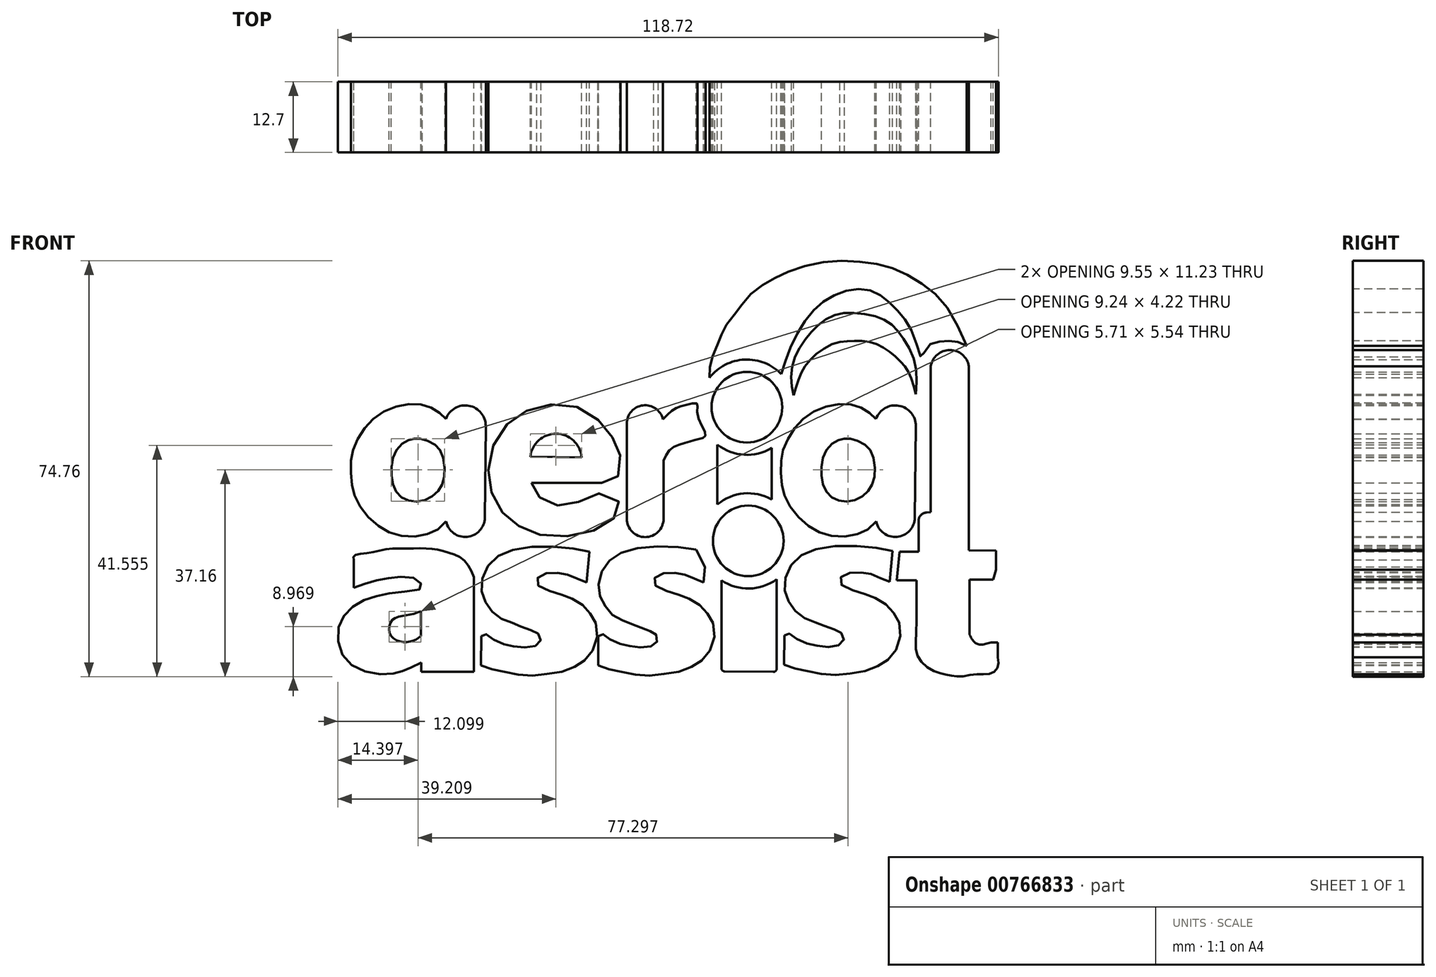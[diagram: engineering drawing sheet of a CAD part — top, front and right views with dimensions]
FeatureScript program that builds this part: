
annotation { "Feature Type Name" : "Feature", "Feature Type Description" : "" }
export const myFeature = defineFeature(function(context is Context, id is Id, definition is map)
    precondition{}
    {
        {
            var Q0;
            Q0=qCreatedBy(makeId("Front.planeOp"),FACE);
            var sketch = newSketch(context, id + "F0", { "sketchPlane" : qUnion([Q0])});
            skFitSpline(sketch, "E0", {"points": [v(-44.08, 9.66) * mm, v(-45.28, 10.79) * mm, v(-47.25, 11.85) * mm, v(-49.88, 12.36) * mm, v(-53.47, 11.74) * mm, v(-56.78, 9.94) * mm, v(-59.07, 7.42) * mm, v(-60.64, 4.45) * mm, v(-61.15, 1.98) * mm, v(-61.1, -1.44) * mm, v(-60.59, -3.9) * mm, v(-58.9, -6.99) * mm, v(-56.1, -9.68) * mm, v(-53.08, -11.2) * mm, v(-49.26, -11.47) * mm, v(-46.18, -10.57) * mm, v(-44.05, -8.78) * mm, v(-41.64, -2.84) * mm], "startDerivative": vector(-26.95, 27.22) * mm, "endDerivative": vector(26.9, 83.07) * mm});
            skArc(sketch, "E1.0.endCap", {"start": v(-37.1, -8.1) * mm, "mid": v(-40.27, -11.57) * mm, "end": v(-44.06, -8.8) * mm});
            skLineSegment(sketch, "E1.0.left", {"start": v(-36.93, 8.34) * mm, "end": v(-37.1, -8.1) * mm});
            skArc(sketch, "E2", {"start": v(-36.93, 8.34) * mm, "mid": v(-39.95, 12.01) * mm, "end": v(-44.08, 9.66) * mm});
            skFitSpline(sketch, "E3", {"points": [v(-49.79, 6.08) * mm, v(-51.15, 5.71) * mm, v(-52.94, 4.16) * mm, v(-53.82, 1.44) * mm, v(-53.77, -1.42) * mm, v(-52.8, -3.75) * mm, v(-51, -4.96) * mm, v(-48.63, -5.16) * mm, v(-46.25, -4.04) * mm, v(-44.89, -2.4) * mm, v(-44.3, 0) * mm, v(-44.8, 3.33) * mm, v(-46.1, 5.03) * mm, v(-48.33, 6) * mm, v(-49.79, 6.08) * mm]});
            skLineSegment(sketch, "E4", {"start": v(-28.93, 2.84) * mm, "end": v(-19.7, 2.74) * mm});
            skArc(sketch, "E5", {"start": v(-19.7, 2.74) * mm, "mid": v(-24.27, 6.97) * mm, "end": v(-28.93, 2.84) * mm});
            skLineSegment(sketch, "E6", {"start": v(-28.74, -1.84) * mm, "end": v(-16.09, -1.84) * mm});
            skFitSpline(sketch, "E7", {"points": [v(-16.09, -1.84) * mm, v(-13.72, -1.34) * mm, v(-12.94, 0) * mm, v(-12.76, 3.12) * mm, v(-13.6, 5.34) * mm, v(-14.98, 7.55) * mm, v(-17.38, 9.96) * mm, v(-20.8, 11.9) * mm, v(-24.86, 12.27) * mm, v(-29.02, 11.34) * mm, v(-31.98, 9.68) * mm, v(-34.57, 6.9) * mm, v(-36.04, 3.12) * mm, v(-36.45, -0.54) * mm, v(-35.92, -3.57) * mm, v(-34.42, -6.54) * mm, v(-32.43, -8.6) * mm, v(-30.06, -10.14) * mm, v(-26.74, -11.31) * mm, v(-22.05, -11.44) * mm, v(-17.68, -10.46) * mm, v(-14.42, -8.64) * mm, v(-13, -7.08) * mm, v(-13.25, -4.86) * mm, v(-16.09, -3.69) * mm, v(-18.98, -4.73) * mm, v(-21.66, -5.77) * mm, v(-24.46, -5.84) * mm, v(-26.74, -4.8) * mm, v(-28.1, -3.5) * mm, v(-28.74, -1.84) * mm], "startDerivative": vector(116.89, 0) * mm, "endDerivative": vector(-21.57, 62.43) * mm});
            skArc(sketch, "E8.0.startCap", {"start": v(-11.58, 8.8) * mm, "mid": v(-8.69, 12.07) * mm, "end": v(-5.08, 9.6) * mm});
            skArc(sketch, "E8.0.endCap", {"start": v(-4.98, -8.32) * mm, "mid": v(-8.28, -11.62) * mm, "end": v(-11.58, -8.32) * mm});
            skLineSegment(sketch, "E8.0.left", {"start": v(-4.98, 2.12) * mm, "end": v(-4.98, -8.32) * mm});
            skLineSegment(sketch, "E8.0.right", {"start": v(-11.58, 8.8) * mm, "end": v(-11.58, -8.32) * mm});
            skFitSpline(sketch, "E9", {"points": [v(-5.08, 9.6) * mm, v(-3.02, 11.46) * mm, v(-0.9, 12.17) * mm, v(1.06, 12.4) * mm, v(1.06, 10.52) * mm, v(2.55, 6.99) * mm, v(2.16, 6.28) * mm, v(0.75, 5.89) * mm, v(-0.98, 5.34) * mm, v(-3.5, 4.4) * mm, v(-4.98, 2.12) * mm], "startDerivative": vector(17.8, 19.08) * mm, "endDerivative": vector(-10.39, -23.26) * mm});
            skCircle(sketch, "E10", {"center": v(10.02, 11.75) * mm, "radius": 6.35 * mm});
            skArc(sketch, "E11", {"start": v(4.7, 5.02) * mm, "mid": v(9.48, 3.2) * mm, "end": v(14.45, 4.42) * mm});
            skFitSpline(sketch, "E12", {"points": [v(3.3, 17.09) * mm, v(3.37, 19.33) * mm, v(4.23, 21.82) * mm, v(5.24, 24.32) * mm, v(6.32, 26.56) * mm, v(8.2, 28.96) * mm, v(10.43, 31.79) * mm, v(13.78, 34.27) * mm, v(17.63, 36.16) * mm, v(23.98, 37.87) * mm, v(30.58, 37.87) * mm, v(35.98, 36.85) * mm, v(40.86, 34.36) * mm, v(45.32, 30.59) * mm, v(49.52, 22.79) * mm], "startDerivative": vector(-2.37, 43.6) * mm, "endDerivative": vector(38.1, -85.11) * mm});
            skFitSpline(sketch, "E13", {"points": [v(49.52, 22.79) * mm, v(47.2, 23.65) * mm, v(44.98, 23.56) * mm, v(42.58, 22.79) * mm, v(41.37, 20.77) * mm, v(40.06, 24.45) * mm, v(37.83, 28.27) * mm, v(35.38, 30.85) * mm, v(32.46, 32.65) * mm, v(28.6, 32.82) * mm, v(24.5, 31.19) * mm, v(21.06, 28.1) * mm, v(17.98, 22.79) * mm, v(16.2, 17.69) * mm], "startDerivative": vector(-37.27, 17.9) * mm, "endDerivative": vector(-16.52, -54.42) * mm});
            skCircle(sketch, "E14", {"center": v(10.24, -12.3) * mm, "radius": 6.35 * mm});
            skArc(sketch, "E15", {"start": v(5.42, -19.38) * mm, "mid": v(10.43, -20.87) * mm, "end": v(15.38, -19.16) * mm});
            skLineSegment(sketch, "E16", {"start": v(4.7, 5.02) * mm, "end": v(4.7, -5.75) * mm});
            skLineSegment(sketch, "E17", {"start": v(14.45, 4.42) * mm, "end": v(14.45, -4.83) * mm});
            skArc(sketch, "E18.trimOffspring", {"start": v(16.2, 17.69) * mm, "mid": v(9.62, 20.32) * mm, "end": v(3.3, 17.09) * mm});
            skLineSegment(sketch, "E19", {"start": v(5.42, -19.38) * mm, "end": v(5.42, -35.14) * mm});
            skLineSegment(sketch, "E20", {"start": v(6.04, -35.77) * mm, "end": v(14.74, -35.86) * mm});
            skLineSegment(sketch, "E21", {"start": v(15.38, -35.23) * mm, "end": v(15.38, -19.16) * mm});
            skPoint(sketch, "E22.visualSharp", {"position": v(5.42, -35.76) * mm});
            skArc(sketch, "E22.filletArc", {"start": v(5.42, -35.14) * mm, "mid": v(5.6, -35.58) * mm, "end": v(6.04, -35.77) * mm});
            skPoint(sketch, "E23.visualSharp", {"position": v(15.38, -35.87) * mm});
            skArc(sketch, "E23.filletArc", {"start": v(14.74, -35.86) * mm, "mid": v(15.19, -35.68) * mm, "end": v(15.38, -35.23) * mm});
            skArc(sketch, "E24.trimOffspring", {"start": v(14.45, -4.83) * mm, "mid": v(9.43, -3.76) * mm, "end": v(4.7, -5.75) * mm});
            skFitSpline(sketch, "E25", {"points": [v(18.39, 13.87) * mm, v(17.96, 17.1) * mm, v(18.7, 20.85) * mm, v(20.64, 24.07) * mm, v(22.9, 26.54) * mm, v(25.9, 28.37) * mm, v(29.55, 28.7) * mm, v(33.63, 27.94) * mm, v(36.32, 26.33) * mm, v(38.36, 23.75) * mm, v(40.29, 19.46) * mm, v(40.4, 14.09) * mm], "startDerivative": vector(-7.7, 37.27) * mm, "endDerivative": vector(-3.75, -50.87) * mm});
            skFitSpline(sketch, "E26", {"points": [v(40.4, 14.09) * mm, v(39.22, 17.74) * mm, v(37.82, 19.78) * mm, v(35.35, 21.93) * mm, v(32.34, 23.43) * mm, v(29.02, 23.64) * mm, v(25.69, 23.22) * mm, v(21.5, 20.42) * mm, v(19.67, 17.63) * mm, v(18.39, 13.87) * mm], "startDerivative": vector(-9.3, 34.22) * mm, "endDerivative": vector(-10.28, -33.52) * mm});
            skFitSpline(sketch, "E27", {"points": [v(33.22, 9.66) * mm, v(32.01, 10.79) * mm, v(30.05, 11.85) * mm, v(27.42, 12.36) * mm, v(23.83, 11.74) * mm, v(20.52, 9.94) * mm, v(18.22, 7.42) * mm, v(16.65, 4.45) * mm, v(16.15, 1.98) * mm, v(16.2, -1.44) * mm, v(16.7, -3.9) * mm, v(18.4, -6.99) * mm, v(21.2, -9.68) * mm, v(24.22, -11.2) * mm, v(28.03, -11.47) * mm, v(31.12, -10.57) * mm, v(33.25, -8.78) * mm, v(35.66, -2.84) * mm], "startDerivative": vector(-26.95, 27.22) * mm, "endDerivative": vector(26.9, 83.07) * mm});
            skArc(sketch, "E28.0.endCap", {"start": v(40.2, -8.1) * mm, "mid": v(37.03, -11.57) * mm, "end": v(33.24, -8.8) * mm});
            skLineSegment(sketch, "E28.0.left", {"start": v(40.37, 8.34) * mm, "end": v(40.2, -8.1) * mm});
            skArc(sketch, "E29", {"start": v(40.37, 8.34) * mm, "mid": v(37.35, 12.01) * mm, "end": v(33.22, 9.66) * mm});
            skFitSpline(sketch, "E30", {"points": [v(27.51, 6.08) * mm, v(26.15, 5.71) * mm, v(24.35, 4.16) * mm, v(23.48, 1.44) * mm, v(23.53, -1.42) * mm, v(24.5, -3.75) * mm, v(26.3, -4.96) * mm, v(28.67, -5.16) * mm, v(31.05, -4.04) * mm, v(32.4, -2.4) * mm, v(33, 0) * mm, v(32.5, 3.33) * mm, v(31.2, 5.03) * mm, v(28.96, 6) * mm, v(27.51, 6.08) * mm]});
            skLineSegment(sketch, "E31", {"start": v(49.9, 19.12) * mm, "end": v(49.9, -13.98) * mm});
            skLineSegment(sketch, "E32", {"start": v(49.9, -13.98) * mm, "end": v(54.8, -14.03) * mm});
            skLineSegment(sketch, "E33", {"start": v(54.8, -14.03) * mm, "end": v(54.8, -17.5) * mm});
            skLineSegment(sketch, "E34", {"start": v(54.8, -17.5) * mm, "end": v(54.29, -19.29) * mm});
            skLineSegment(sketch, "E35", {"start": v(54.29, -19.29) * mm, "end": v(50.04, -19.24) * mm});
            skLineSegment(sketch, "E36", {"start": v(50.04, -19.24) * mm, "end": v(50.04, -29.15) * mm});
            skFitSpline(sketch, "E37", {"points": [v(50.04, -29.15) * mm, v(50.72, -30.31) * mm, v(51.8, -30.93) * mm, v(53.9, -30.54) * mm], "startDerivative": vector(1.89, -4.02) * mm, "endDerivative": vector(5.77, 1.79) * mm});
            skLineSegment(sketch, "E38", {"start": v(53.9, -30.54) * mm, "end": v(55.08, -30.54) * mm});
            skLineSegment(sketch, "E39", {"start": v(55.08, -30.54) * mm, "end": v(55.08, -33.26) * mm});
            skFitSpline(sketch, "E40", {"points": [v(55.08, -33.26) * mm, v(55.08, -35.03) * mm, v(53.74, -36.18) * mm, v(51.24, -36.28) * mm, v(48.22, -36.7) * mm, v(46.13, -36.39) * mm, v(43.74, -35.76) * mm, v(40.82, -33.26) * mm, v(40.4, -29.83) * mm, v(40.5, -19.4) * mm], "startDerivative": vector(3.8, -22.5) * mm, "endDerivative": vector(0.14, 58.8) * mm});
            skLineSegment(sketch, "E41", {"start": v(40.5, -19.4) * mm, "end": v(36.97, -19.4) * mm});
            skLineSegment(sketch, "E42", {"start": v(36.97, -19.4) * mm, "end": v(37.44, -14.23) * mm});
            skLineSegment(sketch, "E43", {"start": v(37.44, -14.23) * mm, "end": v(40.85, -14.23) * mm});
            skLineSegment(sketch, "E44", {"start": v(40.85, -14.23) * mm, "end": v(40.85, -8.72) * mm});
            skArc(sketch, "E45", {"start": v(42.31, -7.18) * mm, "mid": v(41.27, -7.66) * mm, "end": v(40.85, -8.72) * mm});
            skLineSegment(sketch, "E46", {"start": v(42.31, -7.18) * mm, "end": v(43.07, -7.15) * mm});
            skLineSegment(sketch, "E47", {"start": v(43.07, -7.15) * mm, "end": v(43.07, 19.12) * mm});
            skArc(sketch, "E48", {"start": v(49.9, 19.12) * mm, "mid": v(46.49, 22.03) * mm, "end": v(43.07, 19.12) * mm});
            skLineSegment(sketch, "E49", {"start": v(-60.64, -20.7) * mm, "end": v(-60.64, -15.71) * mm});
            skFitSpline(sketch, "E50", {"points": [v(-60.64, -15.71) * mm, v(-60.64, -15) * mm, v(-58.31, -14.49) * mm, v(-54.56, -13.77) * mm, v(-50.16, -13.64) * mm, v(-46.67, -13.7) * mm, v(-43.76, -14.36) * mm, v(-40.91, -15.71) * mm, v(-39.05, -18.82) * mm], "startDerivative": vector(-3.73, 12.95) * mm, "endDerivative": vector(10.17, -25.55) * mm});
            skLineSegment(sketch, "E51", {"start": v(-39.05, -18.82) * mm, "end": v(-39.05, -35.8) * mm});
            skLineSegment(sketch, "E52", {"start": v(-39.05, -35.8) * mm, "end": v(-48.55, -35.8) * mm});
            skLineSegment(sketch, "E53", {"start": v(-48.55, -35.8) * mm, "end": v(-48.55, -34.2) * mm});
            skFitSpline(sketch, "E54", {"points": [v(-48.55, -34.2) * mm, v(-50.61, -35.21) * mm, v(-52.11, -35.74) * mm, v(-53.94, -36.19) * mm, v(-57.72, -36.02) * mm, v(-61.53, -34.2) * mm, v(-63.29, -31.18) * mm, v(-63.29, -27.45) * mm, v(-61.75, -24.96) * mm, v(-59.18, -23.13) * mm, v(-56.1, -22.1) * mm, v(-52.45, -21.52) * mm, v(-48.55, -20.86) * mm, v(-48.55, -20.05) * mm, v(-49.66, -19.03) * mm, v(-52.67, -18.8) * mm, v(-55.38, -19.17) * mm, v(-58.16, -19.83) * mm, v(-60.64, -20.7) * mm], "startDerivative": vector(-42.37, -21.84) * mm, "endDerivative": vector(-44.8, -16.78) * mm});
            skLineSegment(sketch, "E55", {"start": v(-48.57, -24.96) * mm, "end": v(-48.57, -29.43) * mm});
            skFitSpline(sketch, "E56", {"points": [v(-48.57, -29.43) * mm, v(-49.6, -30.09) * mm, v(-50.84, -30.45) * mm, v(-52.45, -30.38) * mm, v(-53.91, -29.43) * mm, v(-54.3, -28.07) * mm, v(-53.86, -26.62) * mm, v(-52.45, -25.91) * mm, v(-50.47, -25.55) * mm, v(-48.57, -24.96) * mm], "startDerivative": vector(-10.07, -7.34) * mm, "endDerivative": vector(14.7, 5.52) * mm});
            skLineSegment(sketch, "E57", {"start": v(-18.32, -14.23) * mm, "end": v(-18.82, -19.78) * mm});
            skLineSegment(sketch, "E58", {"start": v(-37.74, -29.44) * mm, "end": v(-37.79, -34.7) * mm});
            skFitSpline(sketch, "E59", {"points": [v(-37.74, -29.44) * mm, v(-37.45, -29.2) * mm, v(-36.85, -29.1) * mm, v(-35.96, -29.75) * mm, v(-34.1, -30.72) * mm, v(-32.48, -31.14) * mm, v(-30.62, -31.45) * mm, v(-28.48, -31.32) * mm, v(-27.5, -30.82) * mm, v(-27.04, -29.99) * mm, v(-27.4, -29.07) * mm, v(-28.14, -28.63) * mm, v(-29.42, -28.13) * mm, v(-31.17, -27.48) * mm, v(-32.56, -26.9) * mm, v(-34.62, -26.04) * mm, v(-36.17, -24.55) * mm, v(-37.32, -22.58) * mm, v(-37.74, -20.36) * mm, v(-36.89, -17.36) * mm, v(-34.75, -15.04) * mm, v(-30.53, -13.57) * mm, v(-23.16, -13.44) * mm, v(-18.32, -14.23) * mm], "startDerivative": vector(12.94, 13.12) * mm, "endDerivative": vector(65.15, -13.59) * mm});
            skFitSpline(sketch, "E60", {"points": [v(-18.82, -19.78) * mm, v(-20.37, -19.15) * mm, v(-22.05, -18.43) * mm, v(-23.58, -18.1) * mm, v(-25.68, -18.1) * mm, v(-27.32, -18.63) * mm, v(-27.85, -19.78) * mm, v(-26.74, -20.8) * mm, v(-23.9, -21.78) * mm, v(-22.05, -22.43) * mm, v(-19.84, -23.55) * mm, v(-18.32, -25.12) * mm, v(-17.22, -26.9) * mm, v(-16.95, -29.92) * mm, v(-18.32, -32.93) * mm, v(-20.1, -34.44) * mm, v(-22.6, -35.62) * mm, v(-26.2, -36.28) * mm, v(-29.62, -36.54) * mm, v(-33.03, -35.95) * mm, v(-35.59, -35.43) * mm, v(-37.79, -34.7) * mm], "startDerivative": vector(-38, 14.53) * mm, "endDerivative": vector(-45.82, 17.03) * mm});
            skLineSegment(sketch, "E61", {"start": v(2.48, -17) * mm, "end": v(2.23, -19.77) * mm});
            skLineSegment(sketch, "E62", {"start": v(-16.69, -29.44) * mm, "end": v(-16.74, -34.7) * mm});
            skFitSpline(sketch, "E63", {"points": [v(-16.69, -29.44) * mm, v(-16.4, -29.2) * mm, v(-15.8, -29.1) * mm, v(-14.9, -29.75) * mm, v(-13.05, -30.72) * mm, v(-11.43, -31.14) * mm, v(-9.57, -31.45) * mm, v(-7.43, -31.32) * mm, v(-6.46, -30.82) * mm, v(-6, -29.99) * mm, v(-6.36, -29.07) * mm, v(-7.09, -28.63) * mm, v(-8.37, -28.13) * mm, v(-10.12, -27.48) * mm, v(-11.5, -26.9) * mm, v(-13.57, -26.04) * mm, v(-15.12, -24.55) * mm, v(-16.27, -22.58) * mm, v(-16.69, -20.36) * mm, v(-15.84, -17.36) * mm, v(-13.7, -15.04) * mm, v(-9.48, -13.57) * mm, v(-2.11, -13.44) * mm, v(2.73, -14.23) * mm], "startDerivative": vector(12.94, 13.12) * mm, "endDerivative": vector(65.15, -13.59) * mm});
            skFitSpline(sketch, "E64", {"points": [v(2.23, -19.77) * mm, v(0.68, -19.15) * mm, v(-1, -18.43) * mm, v(-2.53, -18.1) * mm, v(-4.63, -18.1) * mm, v(-6.27, -18.63) * mm, v(-6.8, -19.77) * mm, v(-5.69, -20.8) * mm, v(-2.86, -21.78) * mm, v(-1, -22.43) * mm, v(1.2, -23.55) * mm, v(2.73, -25.12) * mm, v(3.83, -26.9) * mm, v(4.1, -29.92) * mm, v(2.73, -32.93) * mm, v(0.95, -34.44) * mm, v(-1.55, -35.62) * mm, v(-5.16, -36.28) * mm, v(-8.57, -36.54) * mm, v(-11.98, -35.95) * mm, v(-14.54, -35.43) * mm, v(-16.74, -34.7) * mm], "startDerivative": vector(-38, 14.53) * mm, "endDerivative": vector(-45.82, 17.03) * mm});
            skLineSegment(sketch, "E65", {"start": v(2.48, -17) * mm, "end": v(0.85, -13.85) * mm});
            skLineSegment(sketch, "E66", {"start": v(36.19, -14.11) * mm, "end": v(35.69, -19.66) * mm});
            skLineSegment(sketch, "E67", {"start": v(16.77, -29.32) * mm, "end": v(16.72, -34.58) * mm});
            skFitSpline(sketch, "E68", {"points": [v(16.77, -29.32) * mm, v(17.06, -29.09) * mm, v(17.66, -28.98) * mm, v(18.55, -29.63) * mm, v(20.4, -30.6) * mm, v(22.03, -31.02) * mm, v(23.88, -31.33) * mm, v(26.03, -31.2) * mm, v(27, -30.7) * mm, v(27.47, -29.87) * mm, v(27.1, -28.95) * mm, v(26.37, -28.5) * mm, v(25.09, -28.01) * mm, v(23.33, -27.36) * mm, v(21.95, -26.78) * mm, v(19.88, -25.92) * mm, v(18.34, -24.43) * mm, v(17.19, -22.47) * mm, v(16.77, -20.24) * mm, v(17.62, -17.24) * mm, v(19.76, -14.93) * mm, v(23.98, -13.46) * mm, v(31.34, -13.32) * mm, v(36.19, -14.11) * mm], "startDerivative": vector(12.94, 13.12) * mm, "endDerivative": vector(65.15, -13.59) * mm});
            skFitSpline(sketch, "E69", {"points": [v(35.69, -19.66) * mm, v(34.14, -19.04) * mm, v(32.46, -18.32) * mm, v(30.92, -17.99) * mm, v(28.82, -17.99) * mm, v(27.18, -18.51) * mm, v(26.66, -19.66) * mm, v(27.77, -20.68) * mm, v(30.6, -21.66) * mm, v(32.46, -22.31) * mm, v(34.66, -23.43) * mm, v(36.19, -25) * mm, v(37.29, -26.78) * mm, v(37.55, -29.8) * mm, v(36.19, -32.82) * mm, v(34.4, -34.33) * mm, v(31.9, -35.5) * mm, v(28.3, -36.16) * mm, v(24.89, -36.43) * mm, v(21.47, -35.84) * mm, v(18.91, -35.31) * mm, v(16.72, -34.58) * mm], "startDerivative": vector(-38, 14.53) * mm, "endDerivative": vector(-45.82, 17.03) * mm});
            skSolve(sketch);
        }
        {
            var Q0;
            Q0 = qSketchRegion(id + "F0", true);
            extrude(context, id + "F1", {"entities" : qUnion([Q0]), "depth" : 12.7 * mm, "offsetDistance" : 25.4 * mm});
        }
    });
